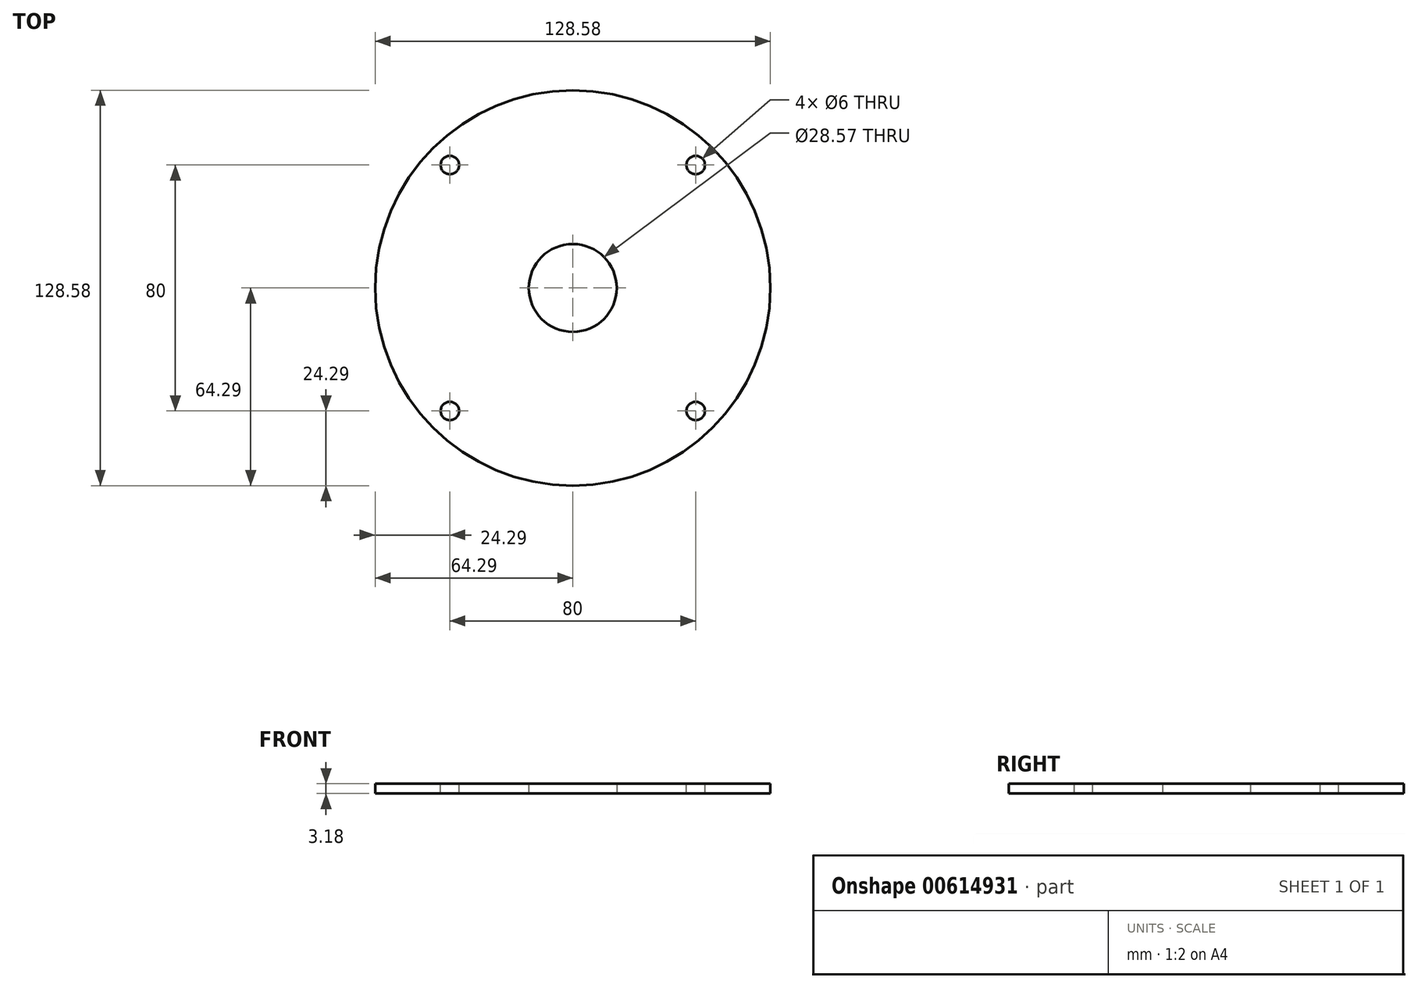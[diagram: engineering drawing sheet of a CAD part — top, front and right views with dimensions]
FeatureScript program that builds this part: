
annotation { "Feature Type Name" : "Feature", "Feature Type Description" : "" }
export const myFeature = defineFeature(function(context is Context, id is Id, definition is map)
    precondition{}
    {
        {
            var Q0;
            Q0=qCreatedBy(makeId("Top.planeOp"),FACE);
            var sketch = newSketch(context, id + "F0", { "sketchPlane" : qUnion([Q0])});
            skCircle(sketch, "E0", {"center": v(0, 0) * mm, "radius": 14.29 * mm});
            skCircle(sketch, "E1", {"center": v(0, 0) * mm, "radius": 64.29 * mm});
            skLineSegment(sketch, "E2", {"start": v(14.29, 0) * mm, "end": v(64.29, 0) * mm});
            skSolve(sketch);
        }
        {
            var Q0;
            Q0 = qSketchRegion(id + "F0", true);
            extrude(context, id + "F1", {"entities" : qUnion([Q0]), "depth" : 0.12 * 25.4 * mm, "offsetDistance" : 25 * mm});
        }
        {
            var Q0;
            Q0=makeQuery(id+"F1.opExtrude","CAP_FACE",FACE,{"disambiguationData":[OSD([sQuery(id+"F0.wireOp",EDGE,"E0"),sQuery(id+"F0.wireOp",EDGE,"E1")])],"isStart":false});
            var sketch = newSketch(context, id + "F2", { "sketchPlane" : qUnion([Q0])});
            skLineSegment(sketch, "E3.bottom", {"start": v(45.5, 45.42) * mm, "end": v(-45.5, 45.42) * mm});
            skLineSegment(sketch, "E3.top", {"start": v(45.5, -45.42) * mm, "end": v(-45.5, -45.42) * mm});
            skLineSegment(sketch, "E3.left", {"start": v(45.5, 45.42) * mm, "end": v(45.5, -45.42) * mm});
            skLineSegment(sketch, "E3.right", {"start": v(-45.5, 45.42) * mm, "end": v(-45.5, -45.42) * mm});
            skPoint(sketch, "E3.middle", {"position": v(0, 0) * mm});
            skLineSegment(sketch, "E4.bottom", {"start": v(40, 40) * mm, "end": v(-40, 40) * mm});
            skLineSegment(sketch, "E4.top", {"start": v(40, -40) * mm, "end": v(-40, -40) * mm});
            skLineSegment(sketch, "E4.left", {"start": v(40, 40) * mm, "end": v(40, -40) * mm});
            skLineSegment(sketch, "E4.right", {"start": v(-40, 40) * mm, "end": v(-40, -40) * mm});
            skCircle(sketch, "E5", {"center": v(-40, 40) * mm, "radius": 3 * mm});
            skCircle(sketch, "E6.MirrorC", {"center": v(40, 40) * mm, "radius": 3 * mm});
            skCircle(sketch, "E7.MirrorC", {"center": v(40, -40) * mm, "radius": 3 * mm});
            skCircle(sketch, "E8.MirrorC", {"center": v(-40, -40) * mm, "radius": 3 * mm});
            skSolve(sketch);
        }
        {
            var Q0;
            {var subQ0=sQuery(id+"F2.wireOp",EDGE,"E4.right");var subQ1=sQuery(id+"F2.wireOp",EDGE,"E4.bottom");var subQ2=makeQuery(id+"F2.imprint","INTERSECT",VERTEX,{"derivedFrom":[subQ1,subQ0]});Q0=makeQuery(id+"F2.imprint","IMPRINT",FACE,{"disambiguationData":[TD([[makeQuery(id+"F2.imprint","IMPRINT",EDGE,{"disambiguationData":[TD([[subQ2,1.0]])],"derivedFrom":subQ1}),1.0]])]});}
            var Q1;
            {var subQ0=sQuery(id+"F2.wireOp",EDGE,"E4.right");var subQ1=sQuery(id+"F2.wireOp",EDGE,"E4.bottom");var subQ2=makeQuery(id+"F2.imprint","INTERSECT",VERTEX,{"derivedFrom":[subQ1,subQ0]});Q1=makeQuery(id+"F2.imprint","IMPRINT",FACE,{"disambiguationData":[TD([[makeQuery(id+"F2.imprint","IMPRINT",EDGE,{"disambiguationData":[TD([[subQ2,1.0]])],"derivedFrom":subQ1}),-1.0]])]});}
            var Q2;
            {var subQ0=sQuery(id+"F2.wireOp",EDGE,"E4.left");var subQ1=sQuery(id+"F2.wireOp",EDGE,"E4.bottom");var subQ2=makeQuery(id+"F2.imprint","INTERSECT",VERTEX,{"derivedFrom":[subQ1,subQ0]});Q2=makeQuery(id+"F2.imprint","IMPRINT",FACE,{"disambiguationData":[TD([[makeQuery(id+"F2.imprint","IMPRINT",EDGE,{"disambiguationData":[TD([[subQ2,-1.0]])],"derivedFrom":subQ1}),1.0]])]});}
            var Q3;
            {var subQ0=sQuery(id+"F2.wireOp",EDGE,"E4.left");var subQ1=sQuery(id+"F2.wireOp",EDGE,"E4.bottom");var subQ2=makeQuery(id+"F2.imprint","INTERSECT",VERTEX,{"derivedFrom":[subQ1,subQ0]});Q3=makeQuery(id+"F2.imprint","IMPRINT",FACE,{"disambiguationData":[TD([[makeQuery(id+"F2.imprint","IMPRINT",EDGE,{"disambiguationData":[TD([[subQ2,-1.0]])],"derivedFrom":subQ1}),-1.0]])]});}
            var Q4;
            {var subQ0=sQuery(id+"F2.wireOp",EDGE,"E4.left");var subQ1=sQuery(id+"F2.wireOp",EDGE,"E4.top");var subQ2=makeQuery(id+"F2.imprint","INTERSECT",VERTEX,{"derivedFrom":[subQ1,subQ0]});Q4=makeQuery(id+"F2.imprint","IMPRINT",FACE,{"disambiguationData":[TD([[makeQuery(id+"F2.imprint","IMPRINT",EDGE,{"disambiguationData":[TD([[subQ2,-1.0]])],"derivedFrom":subQ1}),1.0]])]});}
            var Q5;
            {var subQ0=sQuery(id+"F2.wireOp",EDGE,"E4.left");var subQ1=sQuery(id+"F2.wireOp",EDGE,"E4.top");var subQ2=makeQuery(id+"F2.imprint","INTERSECT",VERTEX,{"derivedFrom":[subQ1,subQ0]});Q5=makeQuery(id+"F2.imprint","IMPRINT",FACE,{"disambiguationData":[TD([[makeQuery(id+"F2.imprint","IMPRINT",EDGE,{"disambiguationData":[TD([[subQ2,-1.0]])],"derivedFrom":subQ1}),-1.0]])]});}
            var Q6;
            {var subQ0=sQuery(id+"F2.wireOp",EDGE,"E4.right");var subQ1=sQuery(id+"F2.wireOp",EDGE,"E4.top");var subQ2=makeQuery(id+"F2.imprint","INTERSECT",VERTEX,{"derivedFrom":[subQ1,subQ0]});Q6=makeQuery(id+"F2.imprint","IMPRINT",FACE,{"disambiguationData":[TD([[makeQuery(id+"F2.imprint","IMPRINT",EDGE,{"disambiguationData":[TD([[subQ2,1.0]])],"derivedFrom":subQ1}),1.0]])]});}
            var Q7;
            {var subQ0=sQuery(id+"F2.wireOp",EDGE,"E4.right");var subQ1=sQuery(id+"F2.wireOp",EDGE,"E4.top");var subQ2=makeQuery(id+"F2.imprint","INTERSECT",VERTEX,{"derivedFrom":[subQ1,subQ0]});Q7=makeQuery(id+"F2.imprint","IMPRINT",FACE,{"disambiguationData":[TD([[makeQuery(id+"F2.imprint","IMPRINT",EDGE,{"disambiguationData":[TD([[subQ2,1.0]])],"derivedFrom":subQ1}),-1.0]])]});}
            extrude(context, id + "F3", {"entities" : qUnion([Q0, Q1, Q2, Q3, Q4, Q5, Q6, Q7]), "operationType" : NewBodyOperationType.REMOVE, "oppositeDirection" : true, "depth" : 25 * mm, "offsetDistance" : 25 * mm});
        }
    });
